# Revit family: 318_044ed59bef4d4a66815dec8506e3e5
name_source: partatom
category: Pipe Accessories
units: mm (PartAtom-declared; Revit-internal decimal feet)

## family parameters
Always vertical = Yes
Cut with Voids When Loaded = No
Part Type = Valve - Normal
Round Connector Dimension = Use Diameter
Shared = No
Work Plane-Based = No

## types (1)
- FAR-3612 11434
    BP = 20 mm
    C = 100 mm  [stored 0.328084 ft]
    CenSd_R_6 = 23 mm
    Description = 1"1/4 Brass modular manifold male-female, 3 port 3/4" female
    L = 295 mm  [stored 0.967848 ft]
    L1 = 31 mm  [stored 0.101706 ft]
    L2 = 4 mm  [stored 0.0131234 ft]
    L3 = 260 mm
    L4 = 20 mm  [stored 0.0656168 ft]
    L5 = 148 mm
    MP1 = 32 mm
    MP2 = 32 mm
    Manufacturer = FAR
    QmdConnectorList = 301;MP1;302;MP2;303;BP;304;BP;305;BP
    R = 26 mm  [stored 0.0853018 ft]
    R1 = 16 mm  [stored 0.0524934 ft]
    R3 = 21 mm  [stored 0.0688976 ft]
    R6 = 11 mm  [stored 0.0360892 ft]
    R8 = 16 mm  [stored 0.0524934 ft]
    URL = www.far.eu
    Z = 34 mm  [stored 0.111549 ft]
    Z__ve = -34 mm  [stored -0.111549 ft]
    magiPartTypeId = 318
    magiProductCode = FAR-3612 11434
    magiProductFamilyId = 044ed59bef4d4a66815dec8506e3e5
    magiProductId = 044ed59bef4d4a66815dec8506e3e5

note: [stored X ft] marks values corroborated as IEEE doubles in the binary element streams (Revit-internal decimal feet)

## geometry (parser evidence)
native form markers: Sweep x2
no freeform markers — native parametric forms only
